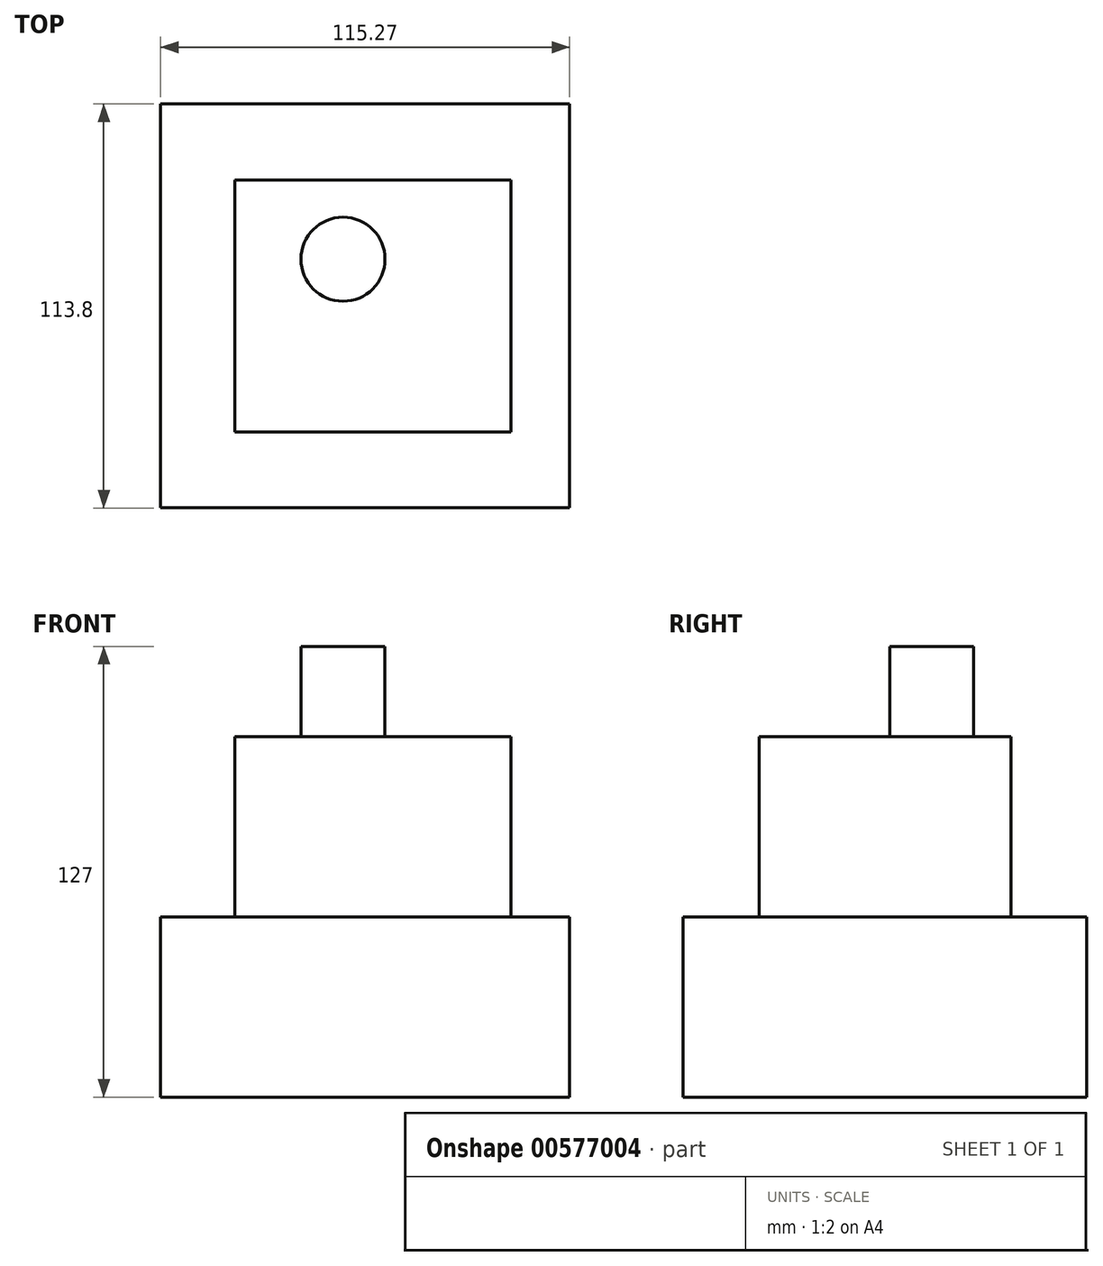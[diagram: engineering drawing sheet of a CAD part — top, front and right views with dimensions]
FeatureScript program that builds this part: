
annotation { "Feature Type Name" : "Feature", "Feature Type Description" : "" }
export const myFeature = defineFeature(function(context is Context, id is Id, definition is map)
    precondition{}
    {
        {
            var Q0;
            Q0=qCreatedBy(makeId("Top.planeOp"),FACE);
            var sketch = newSketch(context, id + "F0", { "sketchPlane" : qUnion([Q0])});
            skLineSegment(sketch, "E0.bottom", {"start": v(50.82, 59.7) * mm, "end": v(-64.45, 59.7) * mm});
            skLineSegment(sketch, "E0.top", {"start": v(50.82, -54.1) * mm, "end": v(-64.45, -54.1) * mm});
            skLineSegment(sketch, "E0.left", {"start": v(50.82, 59.7) * mm, "end": v(50.82, -54.1) * mm});
            skLineSegment(sketch, "E0.right", {"start": v(-64.45, 59.7) * mm, "end": v(-64.45, -54.1) * mm});
            skSolve(sketch);
        }
        {
            var Q0;
            Q0=makeQuery(id+"F0.imprint","IMPRINT",FACE,{"disambiguationData":[TD([[makeQuery(id+"F0.imprint","IMPRINT",EDGE,{"derivedFrom":sQuery(id+"F0.wireOp",EDGE,"E0.bottom")}),1.0]])]});
            extrude(context, id + "F1", {"entities" : qUnion([Q0]), "oppositeDirection" : true, "depth" : 25.4 * mm, "offsetDistance" : 25.4 * mm});
        }
        {
            var Q0;
            Q0=makeQuery(id+"F1.opExtrude","CAP_FACE",FACE,{"disambiguationData":[OSD([sQuery(id+"F0.wireOp",EDGE,"E0.bottom"),sQuery(id+"F0.wireOp",EDGE,"E0.top"),sQuery(id+"F0.wireOp",EDGE,"E0.left"),sQuery(id+"F0.wireOp",EDGE,"E0.right")])],"isStart":false});
            extrude(context, id + "F2", {"entities" : qUnion([Q0]), "operationType" : NewBodyOperationType.ADD, "depth" : 25.4 * mm, "offsetDistance" : 25.4 * mm});
        }
        {
            var Q0;
            Q0=makeQuery(id+"F1.opExtrude","CAP_FACE",FACE,{"disambiguationData":[OSD([sQuery(id+"F0.wireOp",EDGE,"E0.bottom"),sQuery(id+"F0.wireOp",EDGE,"E0.top"),sQuery(id+"F0.wireOp",EDGE,"E0.left"),sQuery(id+"F0.wireOp",EDGE,"E0.right")])],"isStart":true});
            var sketch = newSketch(context, id + "F3", { "sketchPlane" : qUnion([Q0])});
            skLineSegment(sketch, "E1.bottom", {"start": v(-43.6, 38.33) * mm, "end": v(34.35, 38.33) * mm});
            skLineSegment(sketch, "E1.top", {"start": v(-43.6, -32.66) * mm, "end": v(34.35, -32.66) * mm});
            skLineSegment(sketch, "E1.left", {"start": v(-43.6, 38.33) * mm, "end": v(-43.6, -32.66) * mm});
            skLineSegment(sketch, "E1.right", {"start": v(34.35, 38.33) * mm, "end": v(34.35, -32.66) * mm});
            skSolve(sketch);
        }
        {
            var Q0;
            Q0=makeQuery(id+"F3.imprint","IMPRINT",FACE,{"disambiguationData":[TD([[makeQuery(id+"F3.imprint","IMPRINT",EDGE,{"derivedFrom":sQuery(id+"F3.wireOp",EDGE,"E1.bottom")}),-1.0]])]});
            extrude(context, id + "F4", {"entities" : qUnion([Q0]), "operationType" : NewBodyOperationType.ADD, "depth" : 25.4 * mm, "offsetDistance" : 25.4 * mm});
        }
        {
            var Q0;
            Q0=makeQuery(id+"F4.opExtrude","CAP_FACE",FACE,{"disambiguationData":[OSD([sQuery(id+"F3.wireOp",EDGE,"E1.bottom"),sQuery(id+"F3.wireOp",EDGE,"E1.top"),sQuery(id+"F3.wireOp",EDGE,"E1.left"),sQuery(id+"F3.wireOp",EDGE,"E1.right")])],"isStart":false});
            extrude(context, id + "F5", {"entities" : qUnion([Q0]), "operationType" : NewBodyOperationType.ADD, "depth" : 25.4 * mm, "offsetDistance" : 25.4 * mm});
        }
        {
            var Q0;
            Q0=makeQuery(id+"F5.opExtrude","CAP_FACE",FACE,{"disambiguationData":[OSD([sQuery(id+"F3.wireOp",EDGE,"E1.bottom"),sQuery(id+"F3.wireOp",EDGE,"E1.top"),sQuery(id+"F3.wireOp",EDGE,"E1.left"),sQuery(id+"F3.wireOp",EDGE,"E1.right")])],"isStart":false});
            var sketch = newSketch(context, id + "F6", { "sketchPlane" : qUnion([Q0])});
            skCircle(sketch, "E2", {"center": v(-13.04, 15.98) * mm, "radius": 11.85 * mm});
            skSolve(sketch);
        }
        {
            var Q0;
            Q0 = qSketchRegion(id + "F6", true);
            extrude(context, id + "F7", {"entities" : qUnion([Q0]), "operationType" : NewBodyOperationType.ADD, "depth" : 25.4 * mm, "offsetDistance" : 25.4 * mm});
        }
    });
